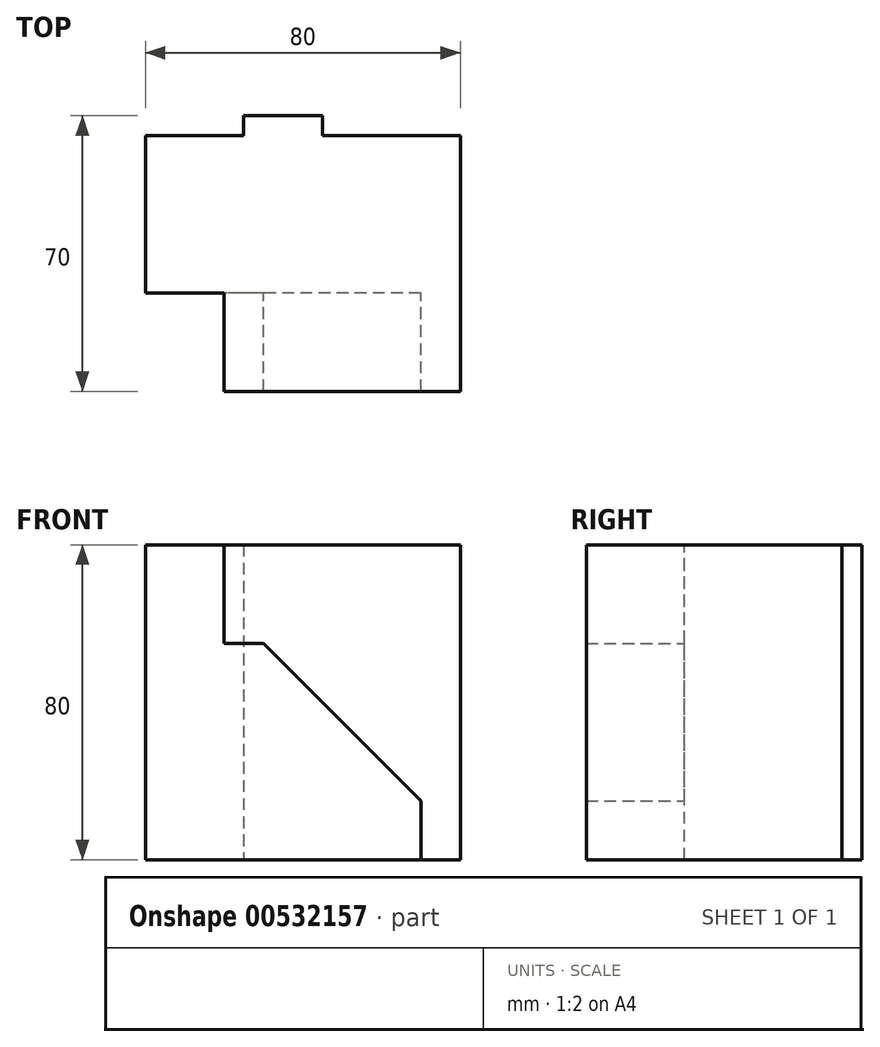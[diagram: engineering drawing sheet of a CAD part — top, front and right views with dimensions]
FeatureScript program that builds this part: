
annotation { "Feature Type Name" : "Feature", "Feature Type Description" : "" }
export const myFeature = defineFeature(function(context is Context, id is Id, definition is map)
    precondition{}
    {
        {
            var Q0;
            Q0=qCreatedBy(makeId("Front.planeOp"),FACE);
            var sketch = newSketch(context, id + "F0", { "sketchPlane" : qUnion([Q0])});
            skLineSegment(sketch, "E0.bottom", {"start": v(40, -40) * mm, "end": v(-40, -40) * mm});
            skLineSegment(sketch, "E0.top", {"start": v(40, 40) * mm, "end": v(-40, 40) * mm});
            skLineSegment(sketch, "E0.left", {"start": v(40, -40) * mm, "end": v(40, 40) * mm});
            skLineSegment(sketch, "E0.right", {"start": v(-40, -40) * mm, "end": v(-40, 40) * mm});
            skPoint(sketch, "E0.middle", {"position": v(0, 0) * mm});
            skSolve(sketch);
        }
        {
            var Q0;
            Q0=makeQuery(id+"F0.imprint","IMPRINT",FACE,{"disambiguationData":[TD([[makeQuery(id+"F0.imprint","IMPRINT",EDGE,{"derivedFrom":sQuery(id+"F0.wireOp",EDGE,"E0.bottom")}),-1.0]])]});
            extrude(context, id + "F1", {"entities" : qUnion([Q0]), "depth" : 45 * mm, "offsetDistance" : 25 * mm});
        }
        {
            var Q0;
            Q0=makeQuery(id+"F1.opExtrude","CAP_FACE",FACE,{"disambiguationData":[OSD([sQuery(id+"F0.wireOp",EDGE,"E0.bottom"),sQuery(id+"F0.wireOp",EDGE,"E0.top"),sQuery(id+"F0.wireOp",EDGE,"E0.left"),sQuery(id+"F0.wireOp",EDGE,"E0.right")])],"isStart":false});
            var sketch = newSketch(context, id + "F2", { "sketchPlane" : qUnion([Q0])});
            skLineSegment(sketch, "E1", {"start": v(-44.32, -25) * mm, "end": v(53.56, -25) * mm, "construction": true});
            skLineSegment(sketch, "E2", {"start": v(30, -40) * mm, "end": v(30, -25) * mm});
            skLineSegment(sketch, "E3", {"start": v(30, -25) * mm, "end": v(-10, 15) * mm});
            skLineSegment(sketch, "E4", {"start": v(30, 53.08) * mm, "end": v(30, -63.92) * mm, "construction": true});
            skLineSegment(sketch, "E5", {"start": v(-10, 15) * mm, "end": v(40, 15) * mm});
            skLineSegment(sketch, "E6", {"start": v(-10, 15) * mm, "end": v(-20, 15) * mm});
            skLineSegment(sketch, "E7", {"start": v(-20, 15) * mm, "end": v(-20, 40) * mm});
            skLineSegment(sketch, "E8", {"start": v(-20, 40) * mm, "end": v(40, 40) * mm});
            skLineSegment(sketch, "E9", {"start": v(40, 40) * mm, "end": v(40, -40) * mm});
            skLineSegment(sketch, "E10", {"start": v(40, -40) * mm, "end": v(30, -40) * mm});
            skLineSegment(sketch, "E11", {"start": v(30, -25) * mm, "end": v(30, -40) * mm});
            skSolve(sketch);
        }
        {
            var Q0;
            Q0=makeQuery(id+"F2.imprint","IMPRINT",FACE,{"disambiguationData":[TD([[makeQuery(id+"F2.imprint","IMPRINT",EDGE,{"derivedFrom":sQuery(id+"F2.wireOp",EDGE,"E3")}),-1.0]])]});
            extrude(context, id + "F3", {"entities" : qUnion([Q0]), "operationType" : NewBodyOperationType.ADD, "depth" : 25 * mm, "offsetDistance" : 25 * mm});
        }
        {
            var Q0;
            Q0=makeQuery(id+"F2.imprint","IMPRINT",FACE,{"disambiguationData":[TD([[makeQuery(id+"F2.imprint","IMPRINT",EDGE,{"derivedFrom":sQuery(id+"F2.wireOp",EDGE,"E6")}),-1.0]])]});
            extrude(context, id + "F4", {"entities" : qUnion([Q0]), "operationType" : NewBodyOperationType.ADD, "depth" : 25 * mm, "offsetDistance" : 25 * mm});
        }
        {
            var Q0;
            Q0=makeQuery(id+"F1.opExtrude","CAP_FACE",FACE,{"disambiguationData":[OSD([sQuery(id+"F0.wireOp",EDGE,"E0.bottom"),sQuery(id+"F0.wireOp",EDGE,"E0.top"),sQuery(id+"F0.wireOp",EDGE,"E0.left"),sQuery(id+"F0.wireOp",EDGE,"E0.right")])],"isStart":true});
            var sketch = newSketch(context, id + "F5", { "sketchPlane" : qUnion([Q0])});
            skLineSegment(sketch, "E12", {"start": v(-5, 40) * mm, "end": v(-5, -40) * mm});
            skLineSegment(sketch, "E13", {"start": v(15, 40) * mm, "end": v(15, -40) * mm});
            skSolve(sketch);
        }
        {
            var Q0;
            {var subQ0=sQuery(id+"F5.wireOp",EDGE,"E12");Q0=makeQuery(id+"F5.imprint","IMPRINT",FACE,{"disambiguationData":[TD([[makeQuery(id+"F5.imprint","IMPRINT",EDGE,{"derivedFrom":subQ0}),-1.0]])]});}
            var Q1;
            {var subQ0=sQuery(id+"F5.wireOp",EDGE,"E13");Q1=makeQuery(id+"F5.imprint","IMPRINT",FACE,{"disambiguationData":[TD([[makeQuery(id+"F5.imprint","IMPRINT",EDGE,{"derivedFrom":subQ0}),1.0]])]});}
            extrude(context, id + "F6", {"entities" : qUnion([Q0, Q1]), "operationType" : NewBodyOperationType.REMOVE, "oppositeDirection" : true, "depth" : 5 * mm, "offsetDistance" : 25 * mm});
        }
    });
